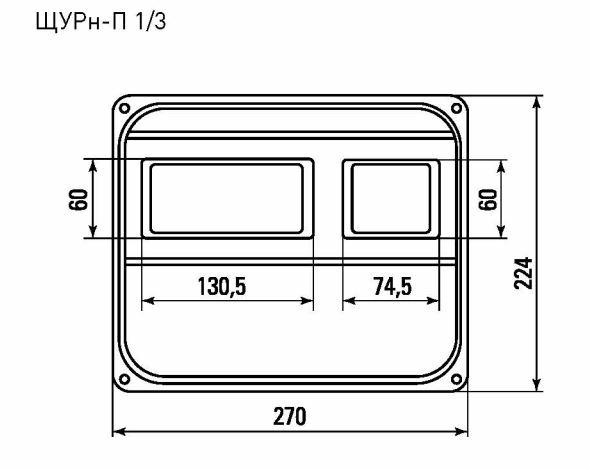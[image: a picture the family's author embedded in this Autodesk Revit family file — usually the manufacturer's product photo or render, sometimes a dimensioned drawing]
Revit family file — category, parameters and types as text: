
# Revit family: EKF_EE_КомплектДляСтыковкиUNIT_PROxima
name_source: partatom
category: Электрооборудование
units: mm (PartAtom-declared; Revit-internal decimal feet)

## family parameters
Всегда вертикально = Нет
На основе рабочей плоскости = Да
Общий = Да
При загрузке вырезать с полостями = Нет
Размер круглого соединителя = Использовать диаметр
Тип детали = Силовой щит
Точка расчета площади = Нет

## types (1)
- Комплект для стыковки ВРУ-1 и ВРУ-2 Unit S IP31
    ADSK_Единица измерения = шт.
    ADSK_Завод-изготовитель = EKF
    ADSK_Код изделия = mb15-08-02-02
    ADSK_Количество = 1
    ADSK_Марка = Комплект для стыковки
    ADSK_Масса = 0
    ADSK_Материал = RAL 7035_Сталь
    ADSK_Наименование = Комплект для стыковки ВРУ-1 и ВРУ-2 Unit S IP31
    ADSK_Обозначение = Комплект для стыковки
    ADSK_Размер_Высота = 0 мм
    ADSK_Размер_Глубина = 0 мм
    ADSK_Размер_Ширина = 0 мм
    D = 10 мм
    Изготовитель = EKF
    Отметка по умолчанию = 0 мм
    Отступ = 20 мм
    Серия номенклатуры = Unit PROxima
    Степень защиты IP = -
    ТВ = EKF_2
    Тип = 19 мм
    Тип установки = -
